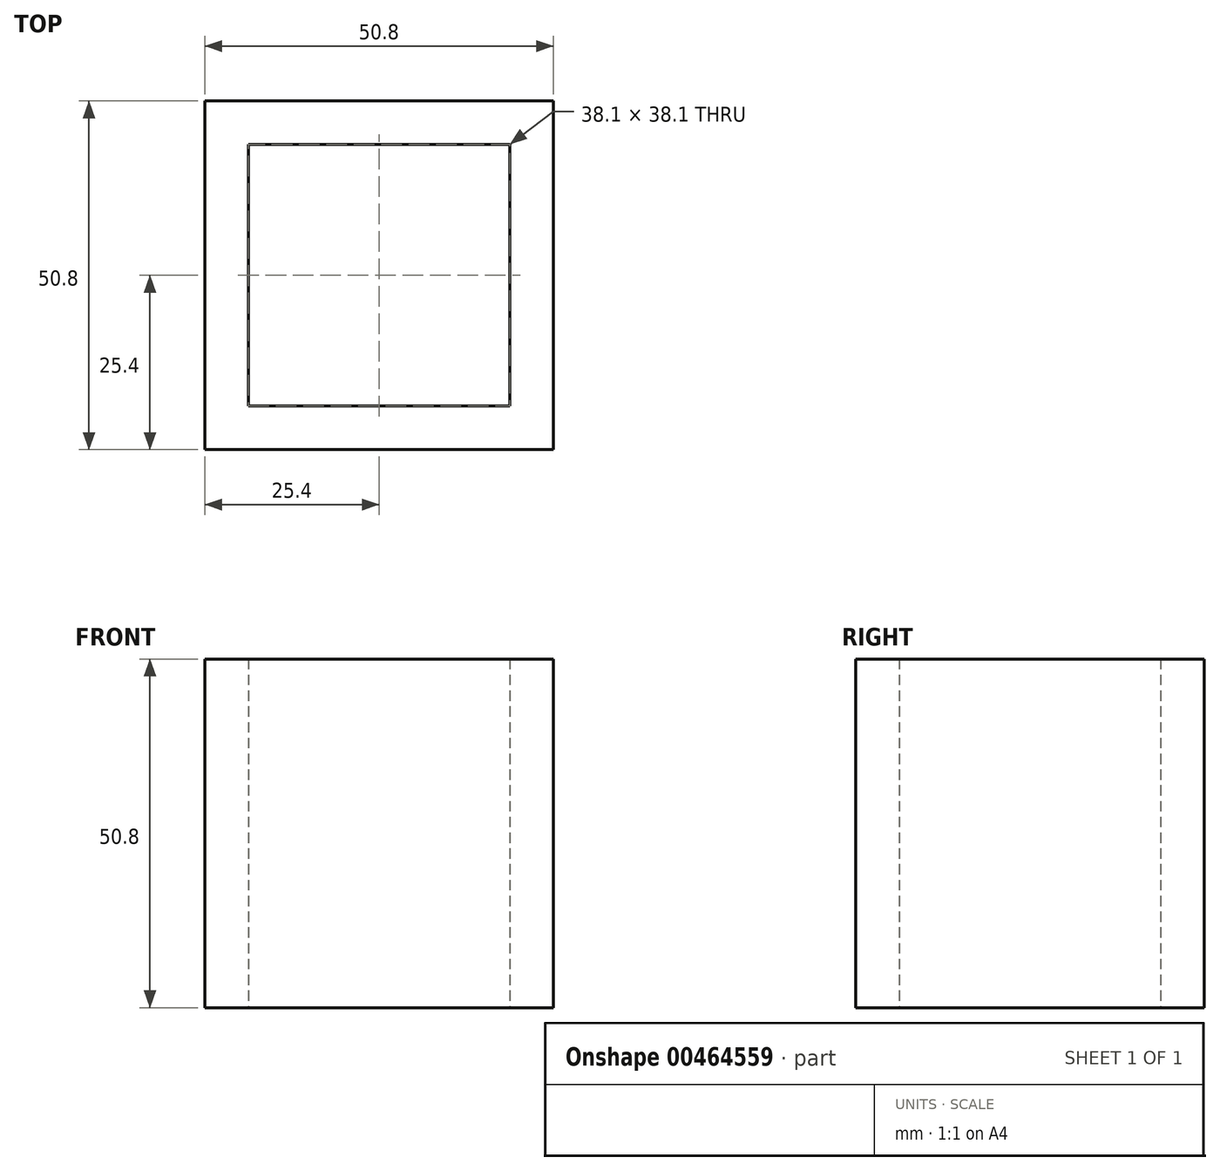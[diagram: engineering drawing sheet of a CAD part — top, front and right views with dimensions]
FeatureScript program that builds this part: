
annotation { "Feature Type Name" : "Feature", "Feature Type Description" : "" }
export const myFeature = defineFeature(function(context is Context, id is Id, definition is map)
    precondition{}
    {
        {
            var Q0;
            Q0=qCreatedBy(makeId("Top.planeOp"),FACE);
            var sketch = newSketch(context, id + "F0", { "sketchPlane" : qUnion([Q0])});
            skLineSegment(sketch, "E0.bottom", {"start": v(0, 0) * mm, "end": v(50.8, 0) * mm});
            skLineSegment(sketch, "E0.top", {"start": v(0, 50.8) * mm, "end": v(50.8, 50.8) * mm});
            skLineSegment(sketch, "E0.left", {"start": v(0, 0) * mm, "end": v(0, 50.8) * mm});
            skLineSegment(sketch, "E0.right", {"start": v(50.8, 0) * mm, "end": v(50.8, 50.8) * mm});
            skLineSegment(sketch, "E1.bottom", {"start": v(6.35, 6.35) * mm, "end": v(44.45, 6.35) * mm});
            skLineSegment(sketch, "E1.top", {"start": v(6.35, 44.45) * mm, "end": v(44.45, 44.45) * mm});
            skLineSegment(sketch, "E1.left", {"start": v(6.35, 6.35) * mm, "end": v(6.35, 44.45) * mm});
            skLineSegment(sketch, "E1.right", {"start": v(44.45, 6.35) * mm, "end": v(44.45, 44.45) * mm});
            skSolve(sketch);
        }
        {
            var Q0;
            Q0=makeQuery(id+"F0.imprint","IMPRINT",FACE,{"disambiguationData":[TD([[makeQuery(id+"F0.imprint","IMPRINT",EDGE,{"derivedFrom":sQuery(id+"F0.wireOp",EDGE,"E0.bottom")}),1.0]])]});
            extrude(context, id + "F1", {"entities" : qUnion([Q0]), "depth" : 50.8 * mm});
        }
    });
